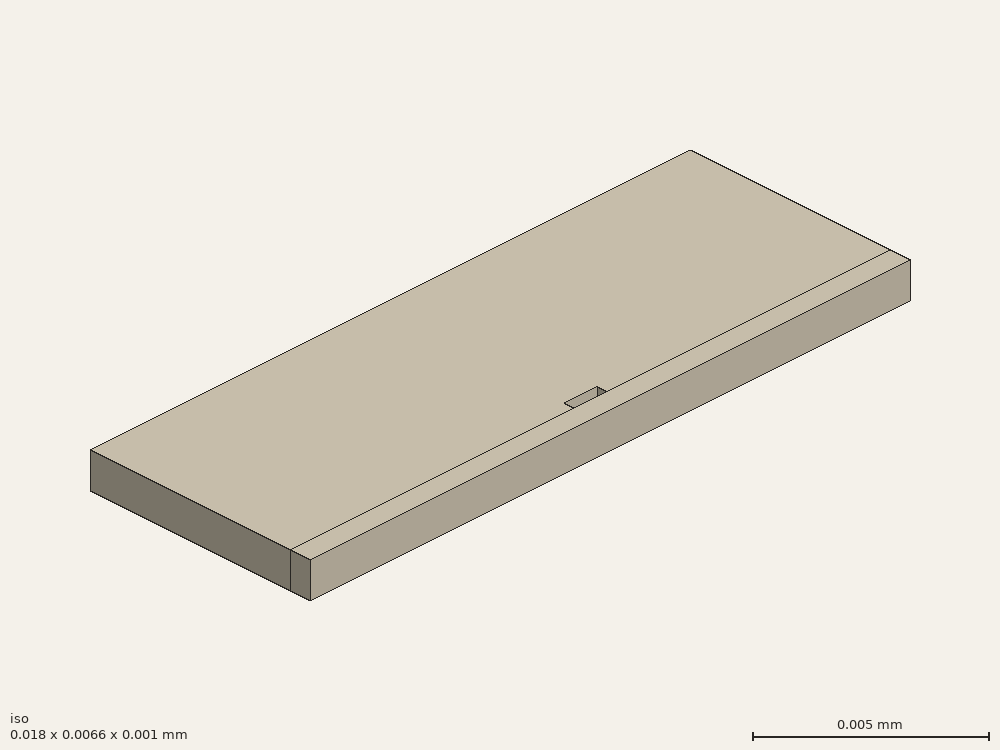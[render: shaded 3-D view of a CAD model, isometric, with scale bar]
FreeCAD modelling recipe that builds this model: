
FCSTD DOCUMENT  (FreeCAD 0.21R33694 (Git))
Label: strip
License: All rights reserved
LicenseURL: http://en.wikipedia.org/wiki/All_rights_reserved
objects: Part::Part2DObjectPython×9, App::FeaturePython×6, Part::Extrusion×3, Part::Cut×1, Part::FeaturePython×1
note: 14 computed .brp shape members not serialized (recipe doc carries the construction recipe); baked Part::Feature solids carry a one-line shape summary decoded from their .brp

FEATURE [Part::Part2DObjectPython] Rectangle  # Draft 2D object (typed FeaturePython)
  Area = 1.143e-05
  ChamferSize = 0
  Columns = 1
  FilletRadius = 0
  Height = 0.000635
  Length = 0.018
  MakeFace = true
  Placement = pos=(-0.009,0,0) rot=(0,0,1;0rad)
  Rows = 1
FEATURE [Part::Part2DObjectPython] Rectangle001  # Draft 2D object (typed FeaturePython)
  Area = 0.000108
  ChamferSize = 0
  Columns = 1
  FilletRadius = 0
  Height = 0.006
  Length = 0.018
  MakeFace = true
  Placement = pos=(-0.009,0.000635,0) rot=(0,0,1;0rad)
  Rows = 1
FEATURE [Part::Part2DObjectPython] Rectangle002  # Draft 2D object (typed FeaturePython)
  Area = 3e-07
  ChamferSize = 0
  Columns = 1
  FilletRadius = 0
  Height = 0.0003
  Length = 0.001
  MakeFace = true
  Placement = pos=(-0.0005,0.000635,0) rot=(0,0,1;0rad)
  Rows = 1
FEATURE [Part::Extrusion] Extrude  label="substrate1"
  Base = -> Rectangle
  Dir = (0,0,1)
  DirMode = 2
  FaceMakerClass = Part::FaceMakerBullseye
  LengthFwd = 0.001
  LengthRev = 0
  Solid = false
  Symmetric = false
FEATURE [Part::Extrusion] Extrude001
  Base = -> Rectangle002
  Dir = (0,0,1)
  DirMode = 2
  FaceMakerClass = Part::FaceMakerBullseye
  LengthFwd = 0.001
  LengthRev = 0
  Solid = false
  Symmetric = false
FEATURE [Part::Extrusion] Extrude002
  Base = -> Rectangle001
  Dir = (0,0,1)
  DirMode = 2
  FaceMakerClass = Part::FaceMakerBullseye
  LengthFwd = 0.001
  LengthRev = 0
  Solid = false
  Symmetric = false
FEATURE [Part::Cut] Cut  label="air1"
  Base = -> Extrude002
  Tool = -> Extrude001
FEATURE [Part::Part2DObjectPython] Rectangle003  label="_Pport1"  # Draft 2D object (typed FeaturePython)
  Area = 0.00011943
  ChamferSize = 0
  Columns = 1
  FilletRadius = 0
  Height = 0.006635
  Length = 0.018
  MakeFace = true
  Placement = pos=(-0.009,0,0.001) rot=(0,0,1;0rad)
  Rows = 1
FEATURE [Part::Part2DObjectPython] Rectangle004  label="_Pi1"  # Draft 2D object (typed FeaturePython)
  Area = 3e-07
  ChamferSize = 0
  Columns = 1
  FilletRadius = 0
  Height = 0.0003
  Length = 0.001
  MakeFace = true
  Placement = pos=(-0.0005,0.000635,0.001) rot=(0,0,1;0rad)
  Rows = 1
FEATURE [Part::Part2DObjectPython] Line  label="_Pv1"  # Draft 2D object (typed FeaturePython)
  Area = 0
  ChamferSize = 0
  Closed = false
  End = (0,0.000635,0.001)
  FilletRadius = 0
  Length = 0.000635
  MakeFace = true
  Placement = pos=(0,0,0.001) rot=(0,0,1;0rad)
  Points = (2) [(0,0,0),(3.88825e-20,0.000635,0)]
  Start = (0,0,0.001)
  Subdivisions = 0
FEATURE [Part::Part2DObjectPython] Rectangle005  label="_Pport2"  # Draft 2D object (typed FeaturePython)
  Area = 0.00011943
  ChamferSize = 0
  Columns = 1
  FilletRadius = 0
  Height = 0.006635
  Length = 0.018
  MakeFace = true
  Placement = pos=(-0.009,0,0) rot=(0,0,1;0rad)
  Rows = 1
FEATURE [Part::Part2DObjectPython] Rectangle006  label="_Pi2"  # Draft 2D object (typed FeaturePython)
  Area = 3e-07
  ChamferSize = 0
  Columns = 1
  FilletRadius = 0
  Height = 0.0003
  Length = 0.001
  MakeFace = true
  Placement = pos=(-0.0005,0.000635,0) rot=(0,0,1;0rad)
  Rows = 1
FEATURE [Part::Part2DObjectPython] Line001  label="_Pv2"  # Draft 2D object (typed FeaturePython)
  Area = 0
  ChamferSize = 0
  Closed = false
  End = (0,0.000635,0)
  FilletRadius = 0
  Length = 0.000635
  MakeFace = true
  Points = (2) [(0,0,0),(1.77361e-18,0.000635,0)]
  Start = (0,0,0)
  Subdivisions = 0
FEATURE [App::FeaturePython] Text  label="_S1(PV){port1}"  # WARN: FeaturePython — macro-defined, semantics opaque (R4)
  Placement = pos=(-0.0005,0.00209073,-0.00864056) rot=(0.57735,0.57735,0.57735;2.0944rad)
  Text = .
FEATURE [App::FeaturePython] Text001  label="_S2(PV){port2}"  # WARN: FeaturePython — macro-defined, semantics opaque (R4)
  Placement = pos=(-0.0005,0.00209073,-0.00864056) rot=(0.57735,0.57735,0.57735;2.0944rad)
  Text = .
FEATURE [App::FeaturePython] Text002  label="_L1(1,voltage){v1}"  # WARN: FeaturePython — macro-defined, semantics opaque (R4)
  Placement = pos=(-0.0005,0.00209073,-0.00864056) rot=(0.57735,0.57735,0.57735;2.0944rad)
  Text = .
FEATURE [App::FeaturePython] Text003  label="_L1(1,current){i1}"  # WARN: FeaturePython — macro-defined, semantics opaque (R4)
  Placement = pos=(-0.0005,0.00209073,-0.00864056) rot=(0.57735,0.57735,0.57735;2.0944rad)
  Text = .
FEATURE [App::FeaturePython] Text004  label="_L2(2,voltage){v2}"  # WARN: FeaturePython — macro-defined, semantics opaque (R4)
  Placement = pos=(-0.0005,0.00209073,-0.00864056) rot=(0.57735,0.57735,0.57735;2.0944rad)
  Text = .
FEATURE [App::FeaturePython] Text005  label="_L2(2,current){i2}"  # WARN: FeaturePython — macro-defined, semantics opaque (R4)
  Placement = pos=(-0.0005,0.00209073,-0.00864056) rot=(0.57735,0.57735,0.57735;2.0944rad)
  Text = .
FEATURE [Part::FeaturePython] BooleanFragments  label="strip"  # WARN: FeaturePython — macro-defined, semantics opaque (R4)
  Mode = 0
  Objects = -> [Extrude,Cut]
  Tolerance = 0
